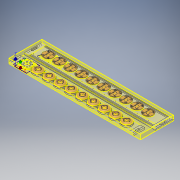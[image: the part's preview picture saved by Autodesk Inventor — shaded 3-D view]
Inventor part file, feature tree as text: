
AUTODESK INVENTOR PART (.ipt)
format: ipt  version: 2018.3 (Build 223284000, 284)  size: 6,967,296 bytes
history: native  units: in
note: dims shown in document units (in); Inventor stores cm internally (conversion verified against a paired STEP export)
features: other x52, extrude x5, pattern_linear x2, sketch x1
ambient origin geometry x8: Origin, YZ Plane, XZ Plane, XY Plane, X Axis, Y Axis, Z Axis, Center Point
bodies: Solid1 (feature_tree), Solid3 (feature_tree), Solid4 (feature_tree), Solid5 (feature_tree), Solid6 (feature_tree), Solid7 (feature_tree), Solid8 (feature_tree), Solid9 (feature_tree), Solid10 (feature_tree), Solid11 (feature_tree), Solid12 (feature_tree), Solid13 (feature_tree), Solid14 (feature_tree), Solid15 (feature_tree), Solid16 (feature_tree), Solid17 (feature_tree), Solid18 (feature_tree), Solid19 (feature_tree), Solid20 (feature_tree), Solid21 (feature_tree)
feature tree (60):
  other  "Pedestal Fixture Assembly.iam"
  other  "Pedestal Fixture Base.ipt:1"
  other  "Pedestal.ipt:1"
  other  "Pedestal.ipt:2"
  other  "Pedestal.ipt:3"
  other  "Pedestal.ipt:4"
  other  "Pedestal.ipt:5"
  other  "Pedestal.ipt:6"
  other  "Pedestal.ipt:7"
  other  "Pedestal.ipt:8"
  other  "Pedestal.ipt:9"
  other  "Pedestal.ipt:10"
  other  "Pedestal.ipt:11"
  other  "Pedestal.ipt:12"
  other  "Pedestal.ipt:13"
  other  "Pedestal.ipt:14"
  other  "Pedestal.ipt:15"
  other  "Pedestal.ipt:16"
  other  "Pedestal.ipt:17"
  other  "Pedestal.ipt:18"
  other  "Pedestal.ipt:19"
  other  "Pedestal.ipt:20"
  extrude  "Extrusion9"  Depth=0.5in TaperAngle=0.0deg
  pattern_linear  "Rectangular Pattern2"  Spacing1=1.0in  [1 undecoded]
  extrude  "Extrusion6"  Depth=0.5in
  extrude  "Extrusion1"  Depth=0.5in
  extrude  "Extrusion8"  Depth=0.3937in
  extrude  "Extrusion7"  Depth=0.5in TaperAngle=0.0deg
  pattern_linear  "Rectangular Pattern1"  Spacing1=0.5in  [1 undecoded]
  other  "Contour Leveling Sketch"
  other  "Base Sketch"
  other  "Contour Solid"
  other  "Vacuum Sketch"
  other  "Origin Sketch"
  other  "Orientation Sketch"
  sketch  "Sketch19"  dims[d0=0.3937in d1=1.0in d2=0.0in d11=1.0in d12=0.0in d13=0.5in d14=0.75in d15=0.7874in d17=4.5in d18=0.3937in d20=1.0in d22=0.0625in d23=0.0in d24=0.5in d25=0.0in d26=3.937in d28=5.06in d29=0.126in d30=0.25in d31=0.247in d32=0.0125in d33=0.0in d34=3.937in d36=5.06in d39=0.5in d40=0.5in d41=2.75in d42=2.75in d43=0.0029in d44=0.0029in d45=0.0029in d46=0.0029in]
  other  "Contour Fixture Peg Holes"
  other  "Top Alignment Sketch"
  other  "CAM Midplane Sketch"
  other  "CAM Midplane Sketch_1"
  other  "CAM Midplane Sketch_2"
  other  "CAM Midplane Sketch_3"
  other  "CAM Midplane Sketch_4"
  other  "CAM Midplane Sketch_5"
  other  "CAM Midplane Sketch_6"
  other  "CAM Midplane Sketch_7"
  other  "Hold down alignment sketch"
  other  "Top Alignment Sketch_1"
  other  "CAM Midplane Sketch_8"
  other  "CAM Midplane Sketch_9"
  other  "CAM Midplane Sketch_10"
  other  "CAM Midplane Sketch_11"
  other  "CAM Midplane Sketch_12"
  other  "CAM Midplane Sketch_13"
  other  "CAM Midplane Sketch_14"
  other  "CAM Midplane Sketch_15"
  other  "CAM Midplane Sketch_16"
  other  "CAM Midplane Sketch_17"
  other  "CAM Midplane Sketch_18"
  other  "CAM Midplane Sketch_19"
note: 2 required parameter values undecoded (feature->parameter linkage not recoverable at this tier; creation-order binding heuristic only, values carry confidence <= 0.55)
